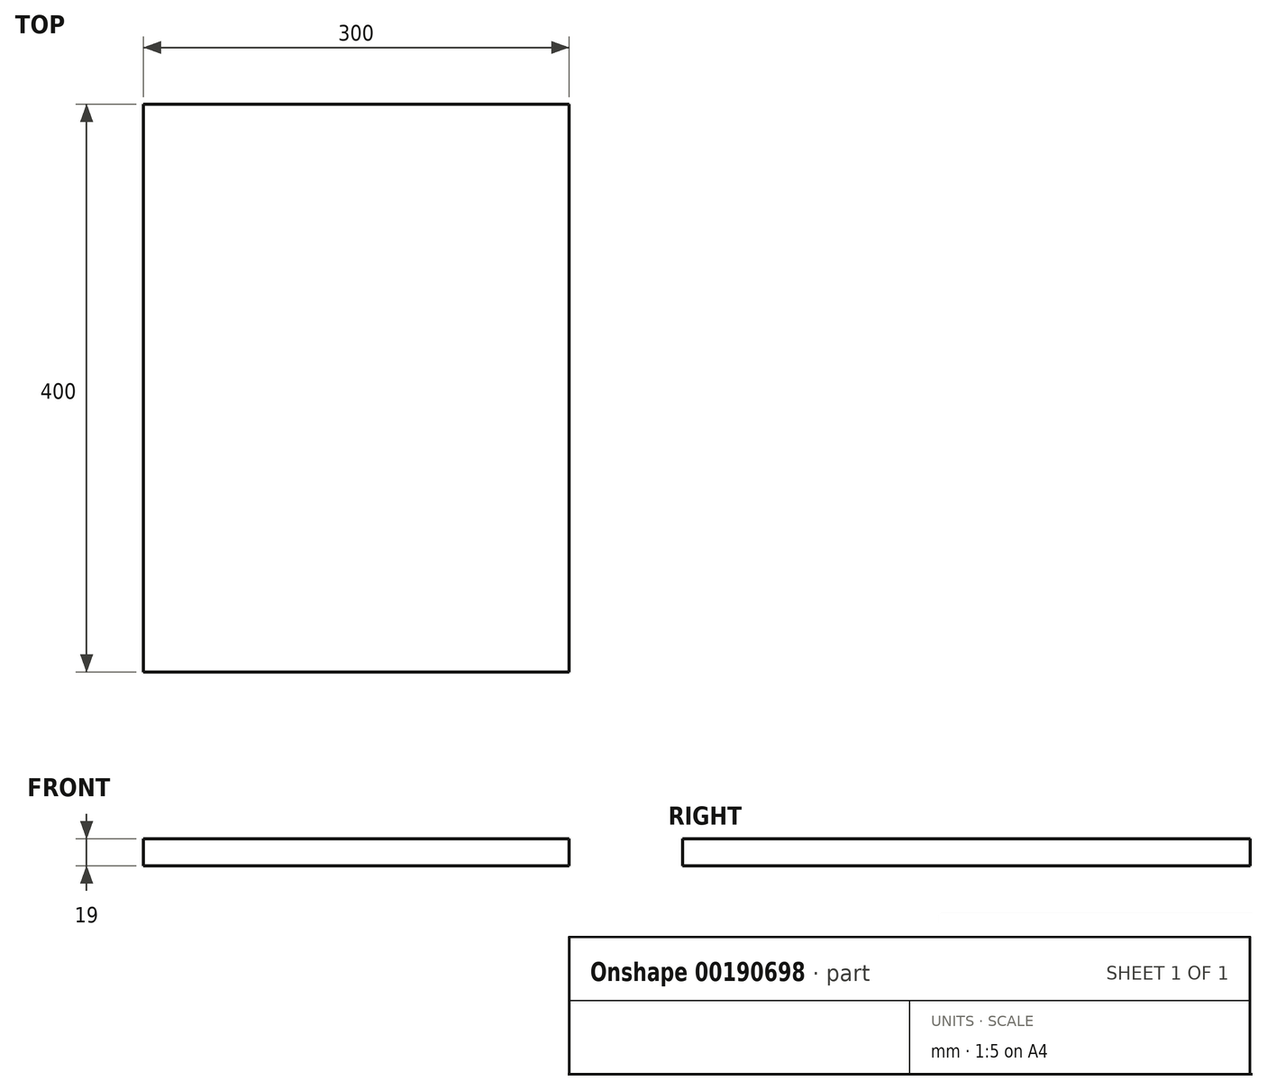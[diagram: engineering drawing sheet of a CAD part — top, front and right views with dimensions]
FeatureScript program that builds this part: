
annotation { "Feature Type Name" : "Feature", "Feature Type Description" : "" }
export const myFeature = defineFeature(function(context is Context, id is Id, definition is map)
    precondition{}
    {
        {
            var Q0;
            Q0=qCreatedBy(makeId("Top.planeOp"),FACE);
            var sketch = newSketch(context, id + "F0", { "sketchPlane" : qUnion([Q0])});
            skLineSegment(sketch, "E0.bottom", {"start": v(-154.57, -166.79) * mm, "end": v(145.43, -166.79) * mm});
            skLineSegment(sketch, "E0.top", {"start": v(-154.57, 233.21) * mm, "end": v(145.43, 233.21) * mm});
            skLineSegment(sketch, "E0.left", {"start": v(-154.57, -166.79) * mm, "end": v(-154.57, 233.21) * mm});
            skLineSegment(sketch, "E0.right", {"start": v(145.43, -166.79) * mm, "end": v(145.43, 233.21) * mm});
            skSolve(sketch);
        }
        {
            var Q0;
            Q0 = qSketchRegion(id + "F0", true);
            extrude(context, id + "F1", {"entities" : qUnion([Q0]), "depth" : 19 * mm});
        }
    });
